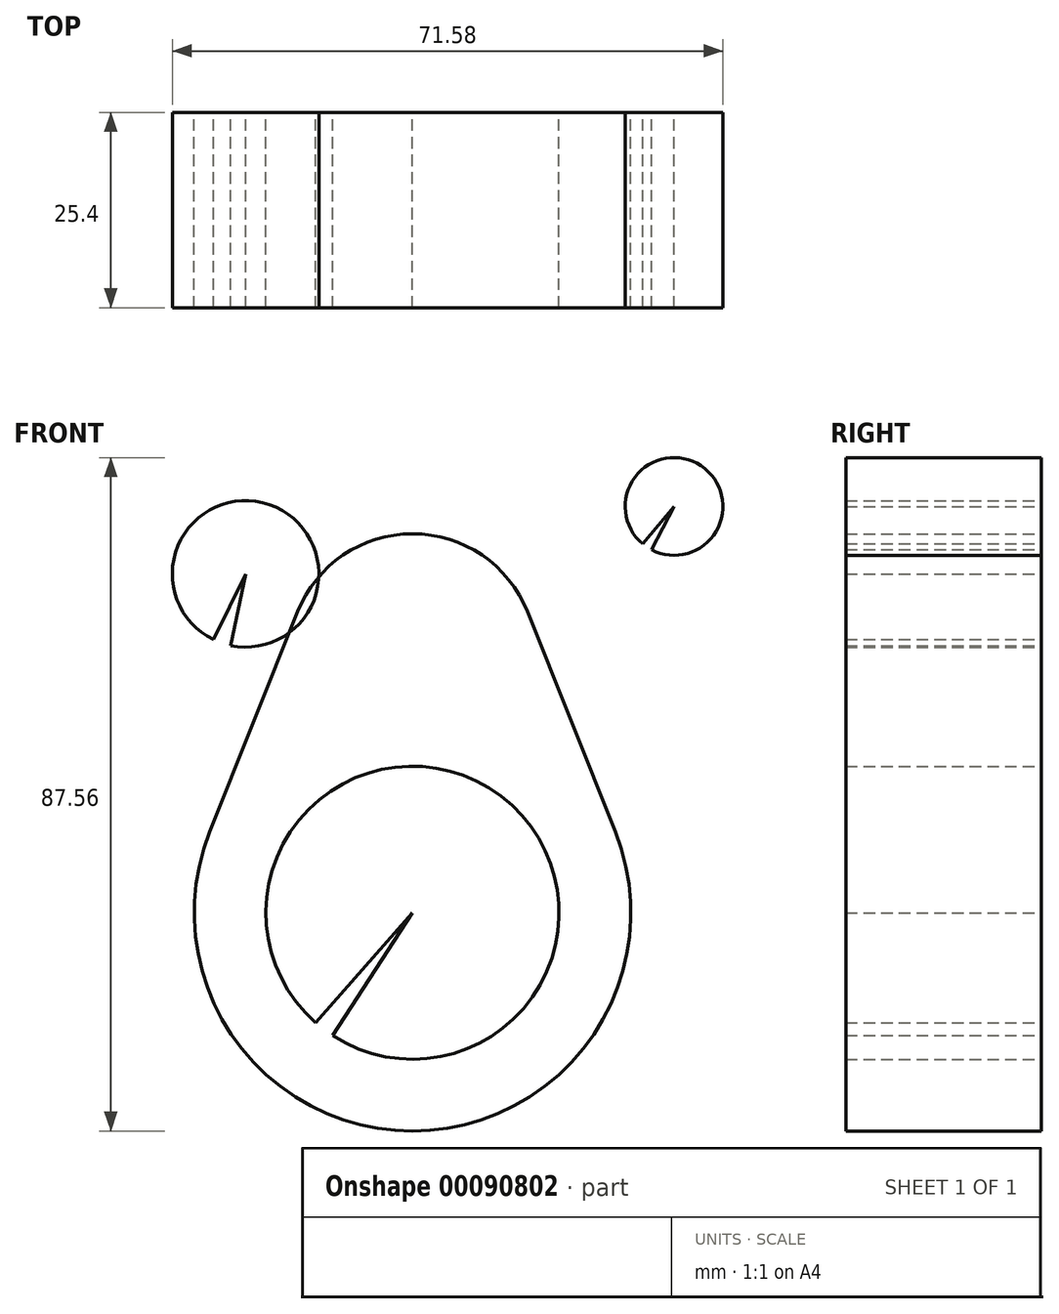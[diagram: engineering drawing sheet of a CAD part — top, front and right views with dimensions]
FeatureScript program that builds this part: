
annotation { "Feature Type Name" : "Feature", "Feature Type Description" : "" }
export const myFeature = defineFeature(function(context is Context, id is Id, definition is map)
    precondition{}
    {
        {
            var Q0;
            Q0=qCreatedBy(makeId("Front.planeOp"),FACE);
            var sketch = newSketch(context, id + "F0", { "sketchPlane" : qUnion([Q0])});
            skArc(sketch, "E0", {"start": v(-10.37, -15.98) * mm, "mid": v(11.5, 15.19) * mm, "end": v(-12.57, -14.31) * mm});
            skArc(sketch, "E1", {"start": v(-23.66, 34.74) * mm, "mid": v(-18.6, 53.07) * mm, "end": v(-25.9, 35.5) * mm});
            skArc(sketch, "E2", {"start": v(31.08, 47.2) * mm, "mid": v(37.52, 58.11) * mm, "end": v(29.93, 47.96) * mm});
            skLineSegment(sketch, "E3", {"start": v(0, 0) * mm, "end": v(-12.57, -14.31) * mm});
            skLineSegment(sketch, "E4", {"start": v(0, 0) * mm, "end": v(-10.37, -15.98) * mm});
            skLineSegment(sketch, "E5", {"start": v(-21.7, 44.06) * mm, "end": v(-25.9, 35.5) * mm});
            skLineSegment(sketch, "E6", {"start": v(34, 52.83) * mm, "end": v(29.93, 47.96) * mm});
            skLineSegment(sketch, "E7", {"start": v(34, 52.83) * mm, "end": v(31.08, 47.2) * mm});
            skLineSegment(sketch, "E8", {"start": v(-23.66, 34.74) * mm, "end": v(-21.7, 44.06) * mm});
            skSolve(sketch);
        }
        {
            var Q0;
            Q0=makeQuery(id+"F0.imprint","IMPRINT",FACE,{"disambiguationData":[TD([[makeQuery(id+"F0.imprint","IMPRINT",EDGE,{"derivedFrom":sQuery(id+"F0.wireOp",EDGE,"E0")}),1.0]])]});
            extrude(context, id + "F1", {"entities" : qUnion([Q0]), "depth" : 25.4 * mm});
        }
        {
            var Q0;
            Q0=makeQuery(id+"F0.imprint","IMPRINT",FACE,{"disambiguationData":[TD([[makeQuery(id+"F0.imprint","IMPRINT",EDGE,{"derivedFrom":sQuery(id+"F0.wireOp",EDGE,"E1")}),1.0]])]});
            extrude(context, id + "F2", {"entities" : qUnion([Q0]), "depth" : 25.4 * mm});
        }
        {
            var Q0;
            Q0=makeQuery(id+"F0.imprint","IMPRINT",FACE,{"disambiguationData":[TD([[makeQuery(id+"F0.imprint","IMPRINT",EDGE,{"derivedFrom":sQuery(id+"F0.wireOp",EDGE,"E2")}),1.0]])]});
            extrude(context, id + "F3", {"entities" : qUnion([Q0]), "depth" : 25.4 * mm});
        }
        {
            var Q0;
            Q0=qCreatedBy(makeId("Front.planeOp"),FACE);
            var sketch = newSketch(context, id + "F4", { "sketchPlane" : qUnion([Q0])});
            skArc(sketch, "E9", {"start": v(-26.36, 10.52) * mm, "mid": v(0, -28.38) * mm, "end": v(26.36, 10.52) * mm});
            skArc(sketch, "E10", {"start": v(14.94, 39.15) * mm, "mid": v(0, 49.27) * mm, "end": v(-14.94, 39.15) * mm});
            skPoint(sketch, "E11.visualSharp", {"position": v(13.74, 24.83) * mm});
            skArc(sketch, "E11.filletArc", {"start": v(14.94, 39.15) * mm, "mid": v(20.65, 24.83) * mm, "end": v(26.36, 10.52) * mm});
            skPoint(sketch, "E12.visualSharp", {"position": v(-13.74, 24.83) * mm});
            skArc(sketch, "E12.filletArc", {"start": v(-26.36, 10.52) * mm, "mid": v(-20.65, 24.83) * mm, "end": v(-14.94, 39.15) * mm});
            skSolve(sketch);
        }
        {
            var Q0;
            Q0 = qSketchRegion(id + "F4", true);
            extrude(context, id + "F5", {"entities" : qUnion([Q0]), "depth" : 25.4 * mm});
        }
    });
